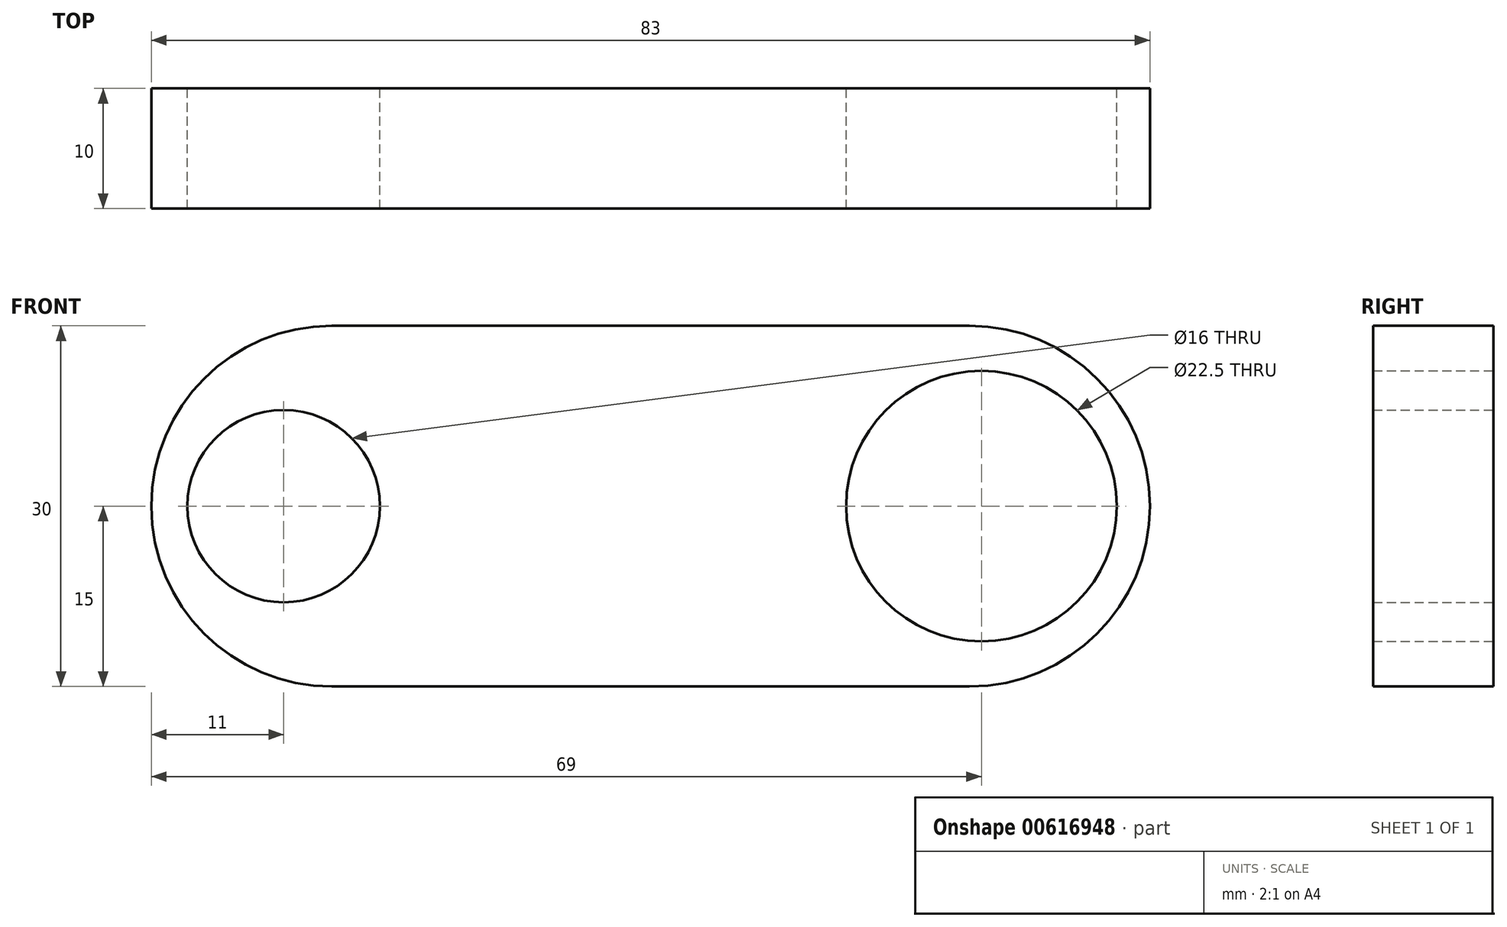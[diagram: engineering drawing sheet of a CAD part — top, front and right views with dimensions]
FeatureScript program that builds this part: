
annotation { "Feature Type Name" : "Feature", "Feature Type Description" : "" }
export const myFeature = defineFeature(function(context is Context, id is Id, definition is map)
    precondition{}
    {
        {
            var Q0;
            Q0=qCreatedBy(makeId("Front.planeOp"),FACE);
            var sketch = newSketch(context, id + "F0", { "sketchPlane" : qUnion([Q0])});
            skLineSegment(sketch, "E0.bottom", {"start": v(26.5, -15) * mm, "end": v(-26.5, -15) * mm});
            skLineSegment(sketch, "E0.top", {"start": v(26.5, 15) * mm, "end": v(-26.5, 15) * mm});
            skLineSegment(sketch, "E0.left", {"start": v(41.5, 0) * mm, "end": v(41.5, 0) * mm});
            skLineSegment(sketch, "E0.right", {"start": v(-41.5, 0) * mm, "end": v(-41.5, 0) * mm});
            skPoint(sketch, "E0.middle", {"position": v(0, 0) * mm});
            skLineSegment(sketch, "E1", {"start": v(-30.5, 15) * mm, "end": v(-30.5, -15) * mm});
            skLineSegment(sketch, "E2", {"start": v(27.5, 15) * mm, "end": v(27.5, -15) * mm});
            skPoint(sketch, "E3", {"position": v(-30.5, 0) * mm});
            skPoint(sketch, "E4", {"position": v(27.5, 0) * mm});
            skCircle(sketch, "E5", {"center": v(-30.5, 0) * mm, "radius": 8 * mm});
            skCircle(sketch, "E6", {"center": v(27.5, 0) * mm, "radius": 11.25 * mm});
            skPoint(sketch, "E7.visualSharp", {"position": v(-41.5, 15) * mm});
            skArc(sketch, "E7.filletArc", {"start": v(-26.5, 15) * mm, "mid": v(-37.1, 10.6) * mm, "end": v(-41.5, 0) * mm});
            skPoint(sketch, "E8.visualSharp", {"position": v(-41.5, -15) * mm});
            skArc(sketch, "E8.filletArc", {"start": v(-41.5, 0) * mm, "mid": v(-37.1, -10.6) * mm, "end": v(-26.5, -15) * mm});
            skPoint(sketch, "E9.visualSharp", {"position": v(41.5, -15) * mm});
            skArc(sketch, "E9.filletArc", {"start": v(26.5, -15) * mm, "mid": v(37.1, -10.6) * mm, "end": v(41.5, 0) * mm});
            skPoint(sketch, "E10.visualSharp", {"position": v(41.5, 15) * mm});
            skArc(sketch, "E10.filletArc", {"start": v(41.5, 0) * mm, "mid": v(37.1, 10.6) * mm, "end": v(26.5, 15) * mm});
            skSolve(sketch);
        }
        {
            var Q0;
            Q0 = qSketchRegion(id + "F0", true);
            extrude(context, id + "F1", {"entities" : qUnion([Q0]), "depth" : 10 * mm, "offsetDistance" : 25 * mm});
        }
    });
